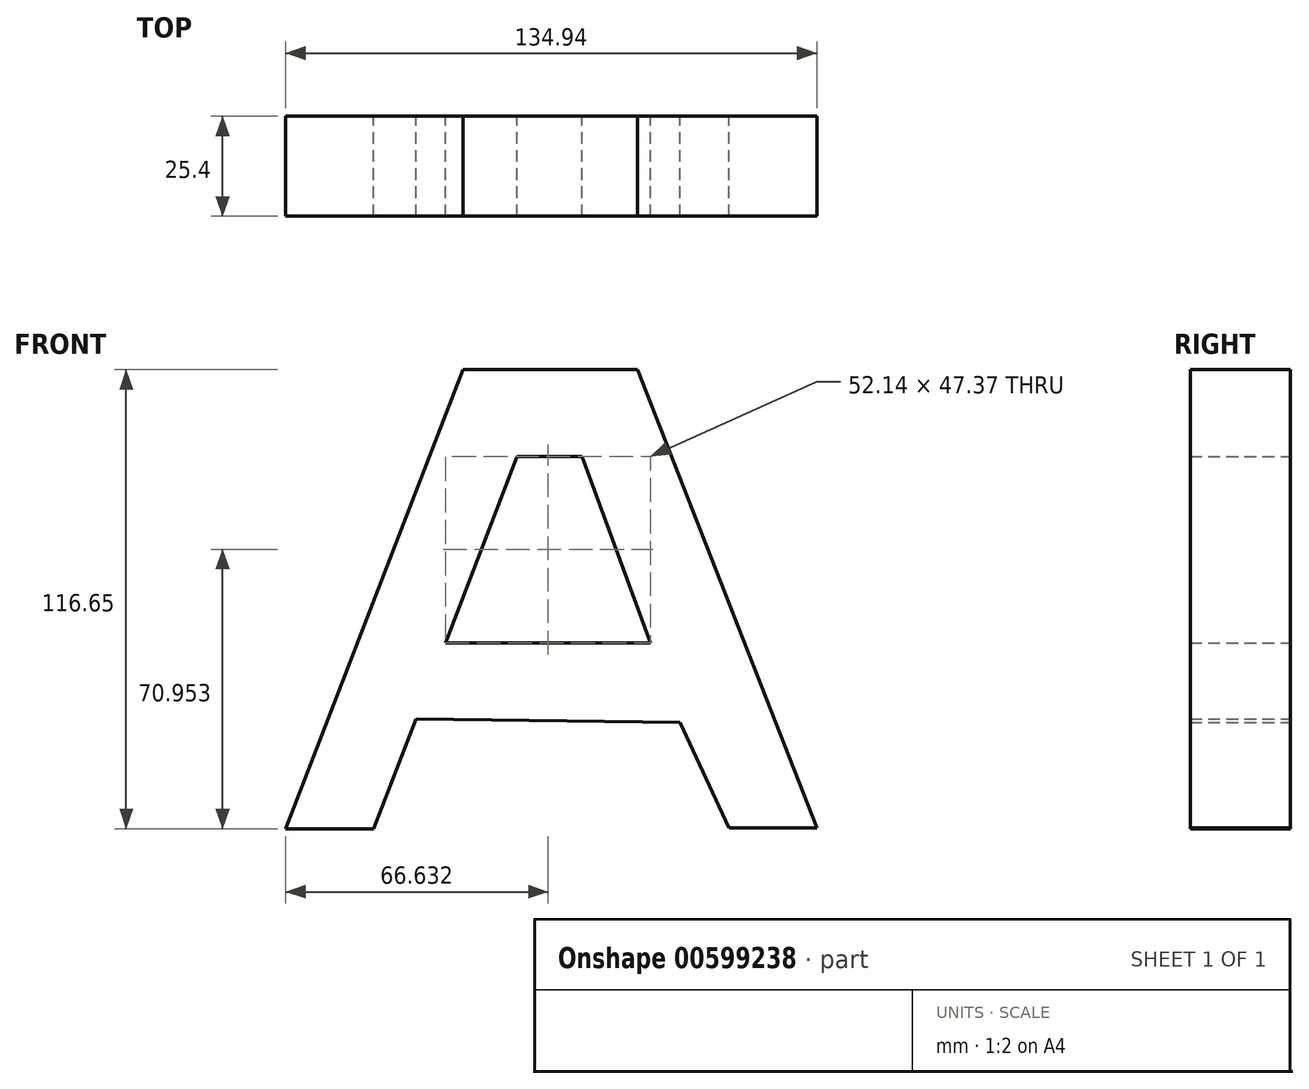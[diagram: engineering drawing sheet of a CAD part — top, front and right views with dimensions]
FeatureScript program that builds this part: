
annotation { "Feature Type Name" : "Feature", "Feature Type Description" : "" }
export const myFeature = defineFeature(function(context is Context, id is Id, definition is map)
    precondition{}
    {
        {
            var Q0;
            Q0=qCreatedBy(makeId("Front.planeOp"),FACE);
            var sketch = newSketch(context, id + "F0", { "sketchPlane" : qUnion([Q0])});
            skLineSegment(sketch, "E0", {"start": v(-34.1, -38.78) * mm, "end": v(-44.87, -66.66) * mm});
            skLineSegment(sketch, "E1", {"start": v(-67.22, -66.66) * mm, "end": v(-22.18, 50) * mm});
            skLineSegment(sketch, "E2", {"start": v(-22.18, 50) * mm, "end": v(0, 50) * mm});
            skLineSegment(sketch, "E3", {"start": v(-67.22, -66.66) * mm, "end": v(-44.87, -66.66) * mm});
            skLineSegment(sketch, "E4", {"start": v(0, 50) * mm, "end": v(22.18, 50) * mm});
            skLineSegment(sketch, "E5", {"start": v(22.18, 50) * mm, "end": v(67.72, -66.46) * mm});
            skLineSegment(sketch, "E6", {"start": v(67.72, -66.46) * mm, "end": v(45.38, -66.46) * mm});
            skLineSegment(sketch, "E7", {"start": v(45.38, -66.46) * mm, "end": v(32.94, -39.7) * mm});
            skLineSegment(sketch, "E8", {"start": v(32.94, -39.7) * mm, "end": v(-34.1, -38.78) * mm});
            skLineSegment(sketch, "E9", {"start": v(25.48, -19.4) * mm, "end": v(-26.66, -19.4) * mm});
            skLineSegment(sketch, "E10", {"start": v(8.08, 27.98) * mm, "end": v(-8.46, 27.98) * mm});
            skLineSegment(sketch, "E11", {"start": v(8.08, 27.98) * mm, "end": v(25.48, -19.4) * mm});
            skLineSegment(sketch, "E12", {"start": v(-8.46, 27.98) * mm, "end": v(-26.66, -19.4) * mm});
            skSolve(sketch);
        }
        {
            var Q0;
            Q0=makeQuery(id+"F0.imprint","IMPRINT",FACE,{"disambiguationData":[TD([[makeQuery(id+"F0.imprint","IMPRINT",EDGE,{"derivedFrom":sQuery(id+"F0.wireOp",EDGE,"E0")}),-1.0]])]});
            extrude(context, id + "F1", {"entities" : qUnion([Q0]), "depth" : 25.4 * mm, "offsetDistance" : 25.4 * mm});
        }
    });
